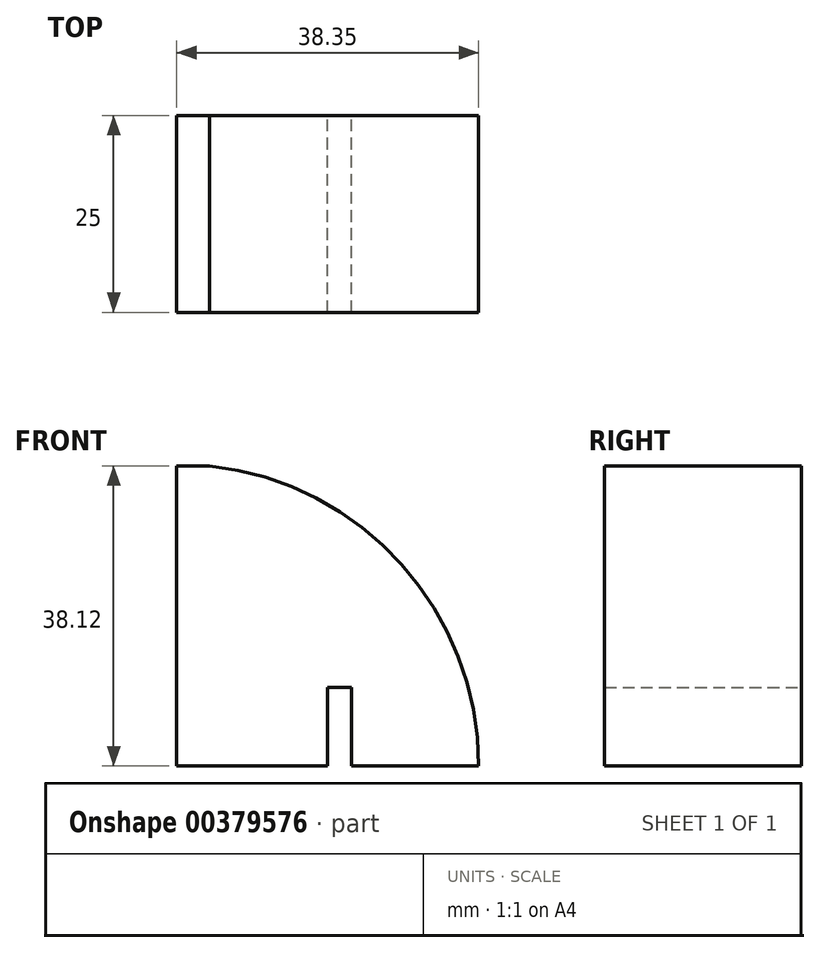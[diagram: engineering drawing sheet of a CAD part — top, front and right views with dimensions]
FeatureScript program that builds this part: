
annotation { "Feature Type Name" : "Feature", "Feature Type Description" : "" }
export const myFeature = defineFeature(function(context is Context, id is Id, definition is map)
    precondition{}
    {
        {
            var Q0;
            Q0=qCreatedBy(makeId("Front.planeOp"),FACE);
            var sketch = newSketch(context, id + "F0", { "sketchPlane" : qUnion([Q0])});
            skLineSegment(sketch, "E0.bottom", {"start": v(0, 0) * mm, "end": v(19.18, 0) * mm});
            skLineSegment(sketch, "E0.top", {"start": v(0, 38.12) * mm, "end": v(4.17, 38.12) * mm});
            skLineSegment(sketch, "E0.left", {"start": v(0, 0) * mm, "end": v(0, 38.12) * mm});
            skArc(sketch, "E1", {"start": v(38.35, 0) * mm, "mid": v(28.56, 25.6) * mm, "end": v(4.17, 38.12) * mm});
            skLineSegment(sketch, "E2.top", {"start": v(19.18, 10) * mm, "end": v(22.18, 10) * mm});
            skLineSegment(sketch, "E2.left", {"start": v(19.18, 0) * mm, "end": v(19.18, 10) * mm});
            skLineSegment(sketch, "E2.right", {"start": v(22.18, 0) * mm, "end": v(22.18, 10) * mm});
            skLineSegment(sketch, "E3.trimOffspring", {"start": v(22.18, 0) * mm, "end": v(38.35, 0) * mm});
            skSolve(sketch);
        }
        {
            var Q0;
            Q0 = qSketchRegion(id + "F0", true);
            extrude(context, id + "F1", {"entities" : qUnion([Q0]), "depth" : 25 * mm});
        }
    });
